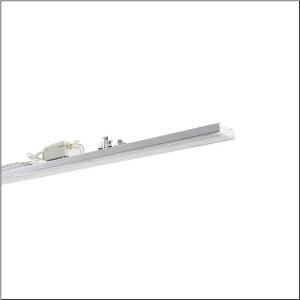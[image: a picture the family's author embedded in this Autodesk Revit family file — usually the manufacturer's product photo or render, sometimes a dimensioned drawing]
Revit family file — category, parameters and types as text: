
# Revit family: licross_r__21_recessed_mo_52te187n485g_b208
name_source: partatom
category: Lighting Fixtures
units: mm (PartAtom-declared; Revit-internal decimal feet)

## family parameters
Cut with Voids When Loaded = No
Host = Face
Light Source = No
Part Type = Normal
Room Calculation Point = No
Round Connector Dimension = Use Diameter
Shared = No

## types (1)
- Licross® 21 Recessed MO (1 x LED, 8570 lm, 47.9 W, 4000K)
    Apparent Load = 48 VA
    CIE Flux Codes = 79 95 99 100 100
    Color Rendering = 80
    Color Temperature = 4000K
    Default Elevation = 1800 mm
    Description = Licross® 21 Recessed MO, luminaire insert, of sheet steel, galvanised, coil coated, white, length: 1.500mm, width: 66mm, height: 67mm, LED rated luminous flux: 8.570lm, light colour: 840, control gear: ON/OFF, with plug, 3-pole, with phase selection, mains connection: 220..240V, AC, 50/60Hz, rated input power: 48W, halogen-free wiring, primary light control with lens, of plastic, primary optical cover: cover, of PMMA, light emission: direct distribution, primary light characteristic: symmetric, protection rating (complete): IP54, insulation class (complete): insulation class I (protective earthing), certification: CE, ENEC, VDE, UKCA, protection symbol: D if used in an environment with non-conductive dust loads with corresponding accessories, impact resistance: IK06, permissible ambient temperature for indoor applications: -35..+40°C, corresponds to IFS (International Featured Standards) requirements for safety and quality in the food industry, reducing of maximum allowable ambient temperature of 5°C with ceiling mounting, LABS conformity tested according to VDMA 24364:2018-05, packaging unit: 1 piece
    Height = 58 mm
    Lamp = 1 x LED
    Lamp Light Flux = 8570 lm
    Lamp Power = 47.9 W
    Lamp count = 1
    Length = 1500 mm
    Luminous efficacy = 179 lm/W
    Manufacturer = Siteco
    ModVariant = No
    Model = 52TE187N485G
    Mounting Place = Ceiling
    Mounting Type = Pendant
    Number of Poles = 1
    OnlyDefault = Yes
    Power Factor = 1
    Product Name = Licross® 21 Recessed MO
    Product group = luminaire insert
    ProductGroupID = 901
    Protection Class = Protection class I
    Protection Degree = IP 54
    RLX_Detail_Level = 1
    RLX_Emergency_Light_Flux = 0 lm
    RLX_Emergency_Type = 0
    RLX_Emergency_Type_DB = No
    RlxData = <blob elided: 20877 chars, md5=5726084a>
    Socket = socket
    Standby Power = 0 W
    System Light Flux = 8570 lm
    System Power = 48 W
    Type Comments = Product without accessories
    Type Image = l_1296930.jpg
    URL = http://relux.com
    VarID = ---
    Voltage = 0 V
    Weight = 0.00 kg
    Width = 66 mm

## geometry (parser evidence)
native form markers: Blend x4, Sweep x9
no freeform markers — native parametric forms only
